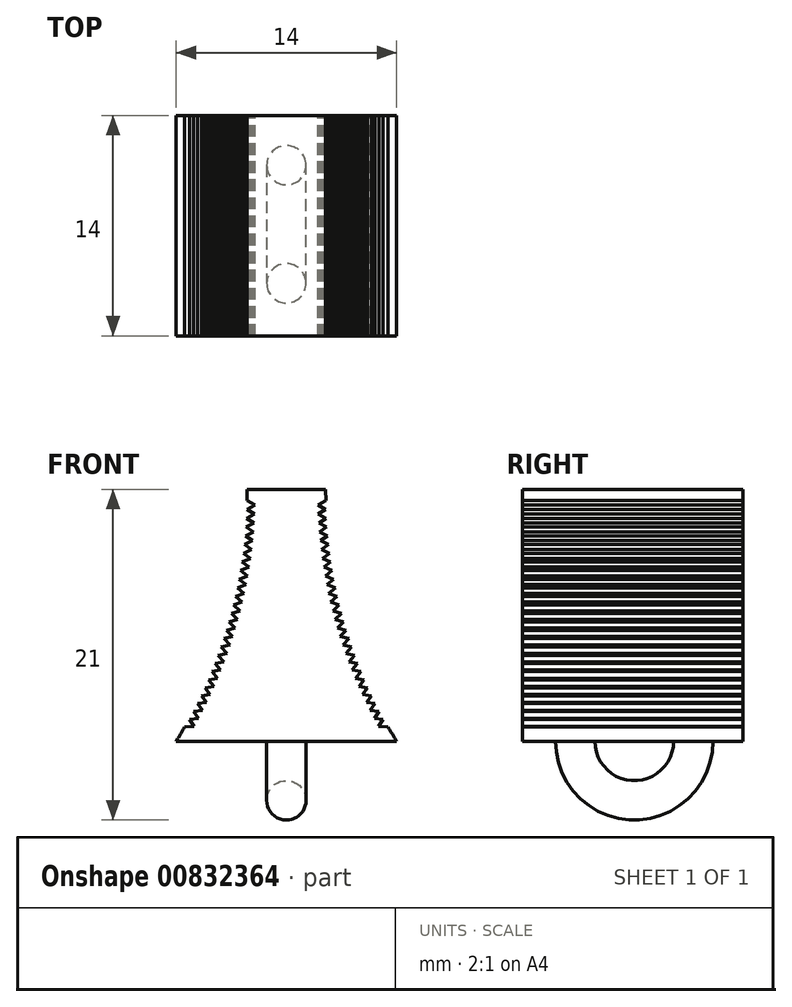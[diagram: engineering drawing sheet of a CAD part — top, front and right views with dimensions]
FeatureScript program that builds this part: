
annotation { "Feature Type Name" : "Feature", "Feature Type Description" : "" }
export const myFeature = defineFeature(function(context is Context, id is Id, definition is map)
    precondition{}
    {
        {
            var Q0;
            Q0=qCreatedBy(makeId("Front.planeOp"),FACE);
            var sketch = newSketch(context, id + "F0", { "sketchPlane" : qUnion([Q0])});
            skLineSegment(sketch, "E0.bottom", {"start": v(-7, -8) * mm, "end": v(7, -8) * mm});
            skLineSegment(sketch, "E0.top", {"start": v(-7, 8) * mm, "end": v(7, 8) * mm});
            skLineSegment(sketch, "E0.left", {"start": v(-7, -8) * mm, "end": v(-7, 8) * mm});
            skLineSegment(sketch, "E0.right", {"start": v(7, -8) * mm, "end": v(7, 8) * mm});
            skPoint(sketch, "E0.middle", {"position": v(0, 0) * mm});
            skArc(sketch, "E1", {"start": v(-7, -8) * mm, "mid": v(-3.65, -0.31) * mm, "end": v(-2.5, 8) * mm});
            skLineSegment(sketch, "E2", {"start": v(0, 8) * mm, "end": v(0, -8) * mm});
            skArc(sketch, "E3.MirrorCS", {"start": v(7, -8) * mm, "mid": v(3.65, -0.31) * mm, "end": v(2.5, 8) * mm});
            skCircle(sketch, "E4.cCircle", {"center": v(7, 7) * mm, "radius": 2.5 * mm, "construction": true});
            skLineSegment(sketch, "E4.0", {"start": v(9.5, 2.67) * mm, "end": v(2, 7) * mm});
            skLineSegment(sketch, "E4.1", {"start": v(2, 7) * mm, "end": v(9.5, 11.33) * mm});
            skLineSegment(sketch, "E4.2", {"start": v(9.5, 11.33) * mm, "end": v(9.5, 2.67) * mm});
            skPoint(sketch, "E4.0.midPoint", {"position": v(5.75, 4.83) * mm});
            skLineSegment(sketch, "E5.MirrorCS", {"start": v(-9.5, 2.67) * mm, "end": v(-2, 7) * mm});
            skLineSegment(sketch, "E6.MirrorCS", {"start": v(-2, 7) * mm, "end": v(-9.5, 11.33) * mm});
            skLineSegment(sketch, "E7.MirrorCS", {"start": v(-9.5, 11.33) * mm, "end": v(-9.5, 2.67) * mm});
            skLineSegment(sketch, "E8.1.0", {"start": v(2.02, 6.43) * mm, "end": v(9.44, 10.9) * mm});
            skLineSegment(sketch, "E8.1.1", {"start": v(9.6, 2.24) * mm, "end": v(2.02, 6.43) * mm});
            skLineSegment(sketch, "E8.1.2", {"start": v(9.44, 10.9) * mm, "end": v(9.6, 2.24) * mm});
            skLineSegment(sketch, "E8.2.0", {"start": v(2.06, 5.87) * mm, "end": v(9.4, 10.47) * mm});
            skLineSegment(sketch, "E8.2.1", {"start": v(9.7, 1.81) * mm, "end": v(2.06, 5.87) * mm});
            skLineSegment(sketch, "E8.2.2", {"start": v(9.4, 10.47) * mm, "end": v(9.7, 1.81) * mm});
            skLineSegment(sketch, "E8.3.0", {"start": v(2.1, 5.3) * mm, "end": v(9.35, 10.04) * mm});
            skLineSegment(sketch, "E8.3.1", {"start": v(9.82, 1.4) * mm, "end": v(2.1, 5.3) * mm});
            skLineSegment(sketch, "E8.3.2", {"start": v(9.35, 10.04) * mm, "end": v(9.82, 1.4) * mm});
            skLineSegment(sketch, "E8.4.0", {"start": v(2.15, 4.74) * mm, "end": v(9.32, 9.6) * mm});
            skLineSegment(sketch, "E8.4.1", {"start": v(9.95, 0.97) * mm, "end": v(2.15, 4.74) * mm});
            skLineSegment(sketch, "E8.4.2", {"start": v(9.32, 9.6) * mm, "end": v(9.95, 0.97) * mm});
            skLineSegment(sketch, "E8.5.0", {"start": v(2.22, 4.18) * mm, "end": v(9.3, 9.17) * mm});
            skLineSegment(sketch, "E8.5.1", {"start": v(10.08, 0.55) * mm, "end": v(2.22, 4.18) * mm});
            skLineSegment(sketch, "E8.5.2", {"start": v(9.3, 9.17) * mm, "end": v(10.08, 0.55) * mm});
            skLineSegment(sketch, "E8.6.0", {"start": v(2.3, 3.62) * mm, "end": v(9.28, 8.74) * mm});
            skLineSegment(sketch, "E8.6.1", {"start": v(10.22, 0.13) * mm, "end": v(2.3, 3.62) * mm});
            skLineSegment(sketch, "E8.6.2", {"start": v(9.28, 8.74) * mm, "end": v(10.22, 0.13) * mm});
            skLineSegment(sketch, "E8.7.0", {"start": v(2.38, 3.06) * mm, "end": v(9.27, 8.3) * mm});
            skLineSegment(sketch, "E8.7.1", {"start": v(10.36, -0.29) * mm, "end": v(2.38, 3.06) * mm});
            skLineSegment(sketch, "E8.7.2", {"start": v(9.27, 8.3) * mm, "end": v(10.36, -0.29) * mm});
            skLineSegment(sketch, "E8.8.0", {"start": v(2.47, 2.5) * mm, "end": v(9.27, 7.87) * mm});
            skLineSegment(sketch, "E8.8.1", {"start": v(10.52, -0.7) * mm, "end": v(2.47, 2.5) * mm});
            skLineSegment(sketch, "E8.8.2", {"start": v(9.27, 7.87) * mm, "end": v(10.52, -0.7) * mm});
            skLineSegment(sketch, "E8.9.0", {"start": v(2.58, 1.95) * mm, "end": v(9.27, 7.44) * mm});
            skLineSegment(sketch, "E8.9.1", {"start": v(10.68, -1.1) * mm, "end": v(2.58, 1.95) * mm});
            skLineSegment(sketch, "E8.9.2", {"start": v(9.27, 7.44) * mm, "end": v(10.68, -1.1) * mm});
            skLineSegment(sketch, "E8.10.0", {"start": v(2.7, 1.4) * mm, "end": v(9.29, 7) * mm});
            skLineSegment(sketch, "E8.10.1", {"start": v(10.85, -1.51) * mm, "end": v(2.7, 1.4) * mm});
            skLineSegment(sketch, "E8.10.2", {"start": v(9.29, 7) * mm, "end": v(10.85, -1.51) * mm});
            skLineSegment(sketch, "E8.11.0", {"start": v(2.82, 0.84) * mm, "end": v(9.3, 6.57) * mm});
            skLineSegment(sketch, "E8.11.1", {"start": v(11.02, -1.92) * mm, "end": v(2.82, 0.84) * mm});
            skLineSegment(sketch, "E8.11.2", {"start": v(9.3, 6.57) * mm, "end": v(11.02, -1.92) * mm});
            skLineSegment(sketch, "E8.12.0", {"start": v(2.95, 0.3) * mm, "end": v(9.34, 6.14) * mm});
            skLineSegment(sketch, "E8.12.1", {"start": v(11.2, -2.32) * mm, "end": v(2.95, 0.3) * mm});
            skLineSegment(sketch, "E8.12.2", {"start": v(9.34, 6.14) * mm, "end": v(11.2, -2.32) * mm});
            skLineSegment(sketch, "E8.13.0", {"start": v(3.1, -0.25) * mm, "end": v(9.38, 5.7) * mm});
            skLineSegment(sketch, "E8.13.1", {"start": v(11.4, -2.71) * mm, "end": v(3.1, -0.25) * mm});
            skLineSegment(sketch, "E8.13.2", {"start": v(9.38, 5.7) * mm, "end": v(11.4, -2.71) * mm});
            skLineSegment(sketch, "E8.14.0", {"start": v(3.25, -0.8) * mm, "end": v(9.42, 5.28) * mm});
            skLineSegment(sketch, "E8.14.1", {"start": v(11.6, -3.1) * mm, "end": v(3.25, -0.8) * mm});
            skLineSegment(sketch, "E8.14.2", {"start": v(9.42, 5.28) * mm, "end": v(11.6, -3.1) * mm});
            skLineSegment(sketch, "E8.15.0", {"start": v(3.41, -1.34) * mm, "end": v(9.48, 4.85) * mm});
            skLineSegment(sketch, "E8.15.1", {"start": v(11.8, -3.5) * mm, "end": v(3.41, -1.34) * mm});
            skLineSegment(sketch, "E8.15.2", {"start": v(9.48, 4.85) * mm, "end": v(11.8, -3.5) * mm});
            skLineSegment(sketch, "E8.16.0", {"start": v(3.59, -1.88) * mm, "end": v(9.54, 4.42) * mm});
            skLineSegment(sketch, "E8.16.1", {"start": v(12.01, -3.88) * mm, "end": v(3.59, -1.88) * mm});
            skLineSegment(sketch, "E8.16.2", {"start": v(9.54, 4.42) * mm, "end": v(12.01, -3.88) * mm});
            skLineSegment(sketch, "E8.17.0", {"start": v(3.77, -2.41) * mm, "end": v(9.6, 3.99) * mm});
            skLineSegment(sketch, "E8.17.1", {"start": v(12.23, -4.26) * mm, "end": v(3.77, -2.41) * mm});
            skLineSegment(sketch, "E8.17.2", {"start": v(9.6, 3.99) * mm, "end": v(12.23, -4.26) * mm});
            skLineSegment(sketch, "E8.18.0", {"start": v(3.97, -2.94) * mm, "end": v(9.68, 3.56) * mm});
            skLineSegment(sketch, "E8.18.1", {"start": v(12.46, -4.64) * mm, "end": v(3.97, -2.94) * mm});
            skLineSegment(sketch, "E8.18.2", {"start": v(9.68, 3.56) * mm, "end": v(12.46, -4.64) * mm});
            skLineSegment(sketch, "E8.19.0", {"start": v(4.17, -3.47) * mm, "end": v(9.77, 3.14) * mm});
            skLineSegment(sketch, "E8.19.1", {"start": v(12.7, -5.02) * mm, "end": v(4.17, -3.47) * mm});
            skLineSegment(sketch, "E8.19.2", {"start": v(9.77, 3.14) * mm, "end": v(12.7, -5.02) * mm});
            skLineSegment(sketch, "E8.20.0", {"start": v(4.38, -4) * mm, "end": v(9.86, 2.71) * mm});
            skLineSegment(sketch, "E8.20.1", {"start": v(12.93, -5.39) * mm, "end": v(4.38, -4) * mm});
            skLineSegment(sketch, "E8.20.2", {"start": v(9.86, 2.71) * mm, "end": v(12.93, -5.39) * mm});
            skLineSegment(sketch, "E8.21.0", {"start": v(4.6, -4.52) * mm, "end": v(9.96, 2.29) * mm});
            skLineSegment(sketch, "E8.21.1", {"start": v(13.18, -5.75) * mm, "end": v(4.6, -4.52) * mm});
            skLineSegment(sketch, "E8.21.2", {"start": v(9.96, 2.29) * mm, "end": v(13.18, -5.75) * mm});
            skLineSegment(sketch, "E8.22.0", {"start": v(4.84, -5.03) * mm, "end": v(10.07, 1.87) * mm});
            skLineSegment(sketch, "E8.22.1", {"start": v(13.43, -6.11) * mm, "end": v(4.84, -5.03) * mm});
            skLineSegment(sketch, "E8.22.2", {"start": v(10.07, 1.87) * mm, "end": v(13.43, -6.11) * mm});
            skLineSegment(sketch, "E8.23.0", {"start": v(5.08, -5.54) * mm, "end": v(10.18, 1.45) * mm});
            skLineSegment(sketch, "E8.23.1", {"start": v(13.69, -6.47) * mm, "end": v(5.08, -5.54) * mm});
            skLineSegment(sketch, "E8.23.2", {"start": v(10.18, 1.45) * mm, "end": v(13.69, -6.47) * mm});
            skLineSegment(sketch, "E8.24.0", {"start": v(5.33, -6.05) * mm, "end": v(10.3, 1.04) * mm});
            skLineSegment(sketch, "E8.24.1", {"start": v(13.95, -6.82) * mm, "end": v(5.33, -6.05) * mm});
            skLineSegment(sketch, "E8.24.2", {"start": v(10.3, 1.04) * mm, "end": v(13.95, -6.82) * mm});
            skLineSegment(sketch, "E8.25.0", {"start": v(5.59, -6.56) * mm, "end": v(10.43, 0.62) * mm});
            skLineSegment(sketch, "E8.25.1", {"start": v(14.22, -7.16) * mm, "end": v(5.59, -6.56) * mm});
            skLineSegment(sketch, "E8.25.2", {"start": v(10.43, 0.62) * mm, "end": v(14.22, -7.16) * mm});
            skLineSegment(sketch, "E8.26.0", {"start": v(5.85, -7.05) * mm, "end": v(10.57, 0.21) * mm});
            skLineSegment(sketch, "E8.26.1", {"start": v(14.5, -7.5) * mm, "end": v(5.85, -7.05) * mm});
            skLineSegment(sketch, "E8.26.2", {"start": v(10.57, 0.21) * mm, "end": v(14.5, -7.5) * mm});
            skLineSegment(sketch, "E8.anchor1", {"start": v(33.2, 8) * mm, "end": v(2, 7) * mm, "construction": true});
            skLineSegment(sketch, "E8.anchor2", {"start": v(33.2, 8) * mm, "end": v(5.85, -7.05) * mm, "construction": true});
            skLineSegment(sketch, "E9.1.0", {"start": v(-9.44, 10.9) * mm, "end": v(-9.6, 2.24) * mm});
            skLineSegment(sketch, "E9.1.1", {"start": v(-9.6, 2.24) * mm, "end": v(-2.02, 6.43) * mm});
            skLineSegment(sketch, "E9.1.2", {"start": v(-2.02, 6.43) * mm, "end": v(-9.44, 10.9) * mm});
            skLineSegment(sketch, "E9.2.0", {"start": v(-9.4, 10.47) * mm, "end": v(-9.7, 1.81) * mm});
            skLineSegment(sketch, "E9.2.1", {"start": v(-9.7, 1.81) * mm, "end": v(-2.06, 5.87) * mm});
            skLineSegment(sketch, "E9.2.2", {"start": v(-2.06, 5.87) * mm, "end": v(-9.4, 10.47) * mm});
            skLineSegment(sketch, "E9.3.0", {"start": v(-9.35, 10.04) * mm, "end": v(-9.82, 1.4) * mm});
            skLineSegment(sketch, "E9.3.1", {"start": v(-9.82, 1.4) * mm, "end": v(-2.1, 5.3) * mm});
            skLineSegment(sketch, "E9.3.2", {"start": v(-2.1, 5.3) * mm, "end": v(-9.35, 10.04) * mm});
            skLineSegment(sketch, "E9.4.0", {"start": v(-9.32, 9.6) * mm, "end": v(-9.95, 0.97) * mm});
            skLineSegment(sketch, "E9.4.1", {"start": v(-9.95, 0.97) * mm, "end": v(-2.15, 4.74) * mm});
            skLineSegment(sketch, "E9.4.2", {"start": v(-2.15, 4.74) * mm, "end": v(-9.32, 9.6) * mm});
            skLineSegment(sketch, "E9.5.0", {"start": v(-9.3, 9.17) * mm, "end": v(-10.08, 0.55) * mm});
            skLineSegment(sketch, "E9.5.1", {"start": v(-10.08, 0.55) * mm, "end": v(-2.22, 4.18) * mm});
            skLineSegment(sketch, "E9.5.2", {"start": v(-2.22, 4.18) * mm, "end": v(-9.3, 9.17) * mm});
            skLineSegment(sketch, "E9.6.0", {"start": v(-9.28, 8.74) * mm, "end": v(-10.22, 0.13) * mm});
            skLineSegment(sketch, "E9.6.1", {"start": v(-10.22, 0.13) * mm, "end": v(-2.3, 3.62) * mm});
            skLineSegment(sketch, "E9.6.2", {"start": v(-2.3, 3.62) * mm, "end": v(-9.28, 8.74) * mm});
            skLineSegment(sketch, "E9.7.0", {"start": v(-9.27, 8.3) * mm, "end": v(-10.36, -0.29) * mm});
            skLineSegment(sketch, "E9.7.1", {"start": v(-10.36, -0.29) * mm, "end": v(-2.38, 3.06) * mm});
            skLineSegment(sketch, "E9.7.2", {"start": v(-2.38, 3.06) * mm, "end": v(-9.27, 8.3) * mm});
            skLineSegment(sketch, "E9.8.0", {"start": v(-9.27, 7.87) * mm, "end": v(-10.52, -0.7) * mm});
            skLineSegment(sketch, "E9.8.1", {"start": v(-10.52, -0.7) * mm, "end": v(-2.47, 2.5) * mm});
            skLineSegment(sketch, "E9.8.2", {"start": v(-2.47, 2.5) * mm, "end": v(-9.27, 7.87) * mm});
            skLineSegment(sketch, "E9.9.0", {"start": v(-9.27, 7.44) * mm, "end": v(-10.68, -1.1) * mm});
            skLineSegment(sketch, "E9.9.1", {"start": v(-10.68, -1.1) * mm, "end": v(-2.58, 1.95) * mm});
            skLineSegment(sketch, "E9.9.2", {"start": v(-2.58, 1.95) * mm, "end": v(-9.27, 7.44) * mm});
            skLineSegment(sketch, "E9.10.0", {"start": v(-9.29, 7) * mm, "end": v(-10.85, -1.51) * mm});
            skLineSegment(sketch, "E9.10.1", {"start": v(-10.85, -1.51) * mm, "end": v(-2.7, 1.4) * mm});
            skLineSegment(sketch, "E9.10.2", {"start": v(-2.7, 1.4) * mm, "end": v(-9.29, 7) * mm});
            skLineSegment(sketch, "E9.11.0", {"start": v(-9.3, 6.57) * mm, "end": v(-11.02, -1.92) * mm});
            skLineSegment(sketch, "E9.11.1", {"start": v(-11.02, -1.92) * mm, "end": v(-2.82, 0.84) * mm});
            skLineSegment(sketch, "E9.11.2", {"start": v(-2.82, 0.84) * mm, "end": v(-9.3, 6.57) * mm});
            skLineSegment(sketch, "E9.12.0", {"start": v(-9.34, 6.14) * mm, "end": v(-11.2, -2.32) * mm});
            skLineSegment(sketch, "E9.12.1", {"start": v(-11.2, -2.32) * mm, "end": v(-2.95, 0.3) * mm});
            skLineSegment(sketch, "E9.12.2", {"start": v(-2.95, 0.3) * mm, "end": v(-9.34, 6.14) * mm});
            skLineSegment(sketch, "E9.13.0", {"start": v(-9.38, 5.7) * mm, "end": v(-11.4, -2.71) * mm});
            skLineSegment(sketch, "E9.13.1", {"start": v(-11.4, -2.71) * mm, "end": v(-3.1, -0.25) * mm});
            skLineSegment(sketch, "E9.13.2", {"start": v(-3.1, -0.25) * mm, "end": v(-9.38, 5.7) * mm});
            skLineSegment(sketch, "E9.14.0", {"start": v(-9.42, 5.28) * mm, "end": v(-11.6, -3.1) * mm});
            skLineSegment(sketch, "E9.14.1", {"start": v(-11.6, -3.1) * mm, "end": v(-3.25, -0.8) * mm});
            skLineSegment(sketch, "E9.14.2", {"start": v(-3.25, -0.8) * mm, "end": v(-9.42, 5.28) * mm});
            skLineSegment(sketch, "E9.15.0", {"start": v(-9.48, 4.85) * mm, "end": v(-11.8, -3.5) * mm});
            skLineSegment(sketch, "E9.15.1", {"start": v(-11.8, -3.5) * mm, "end": v(-3.41, -1.34) * mm});
            skLineSegment(sketch, "E9.15.2", {"start": v(-3.41, -1.34) * mm, "end": v(-9.48, 4.85) * mm});
            skLineSegment(sketch, "E9.16.0", {"start": v(-9.54, 4.42) * mm, "end": v(-12.01, -3.88) * mm});
            skLineSegment(sketch, "E9.16.1", {"start": v(-12.01, -3.88) * mm, "end": v(-3.59, -1.88) * mm});
            skLineSegment(sketch, "E9.16.2", {"start": v(-3.59, -1.88) * mm, "end": v(-9.54, 4.42) * mm});
            skLineSegment(sketch, "E9.17.0", {"start": v(-9.6, 3.99) * mm, "end": v(-12.23, -4.26) * mm});
            skLineSegment(sketch, "E9.17.1", {"start": v(-12.23, -4.26) * mm, "end": v(-3.77, -2.41) * mm});
            skLineSegment(sketch, "E9.17.2", {"start": v(-3.77, -2.41) * mm, "end": v(-9.6, 3.99) * mm});
            skLineSegment(sketch, "E9.18.0", {"start": v(-9.68, 3.56) * mm, "end": v(-12.46, -4.64) * mm});
            skLineSegment(sketch, "E9.18.1", {"start": v(-12.46, -4.64) * mm, "end": v(-3.97, -2.94) * mm});
            skLineSegment(sketch, "E9.18.2", {"start": v(-3.97, -2.94) * mm, "end": v(-9.68, 3.56) * mm});
            skLineSegment(sketch, "E9.19.0", {"start": v(-9.77, 3.14) * mm, "end": v(-12.7, -5.02) * mm});
            skLineSegment(sketch, "E9.19.1", {"start": v(-12.7, -5.02) * mm, "end": v(-4.17, -3.47) * mm});
            skLineSegment(sketch, "E9.19.2", {"start": v(-4.17, -3.47) * mm, "end": v(-9.77, 3.14) * mm});
            skLineSegment(sketch, "E9.20.0", {"start": v(-9.86, 2.71) * mm, "end": v(-12.93, -5.39) * mm});
            skLineSegment(sketch, "E9.20.1", {"start": v(-12.93, -5.39) * mm, "end": v(-4.38, -4) * mm});
            skLineSegment(sketch, "E9.20.2", {"start": v(-4.38, -4) * mm, "end": v(-9.86, 2.71) * mm});
            skLineSegment(sketch, "E9.21.0", {"start": v(-9.96, 2.29) * mm, "end": v(-13.18, -5.75) * mm});
            skLineSegment(sketch, "E9.21.1", {"start": v(-13.18, -5.75) * mm, "end": v(-4.6, -4.52) * mm});
            skLineSegment(sketch, "E9.21.2", {"start": v(-4.6, -4.52) * mm, "end": v(-9.96, 2.29) * mm});
            skLineSegment(sketch, "E9.22.0", {"start": v(-10.07, 1.87) * mm, "end": v(-13.43, -6.11) * mm});
            skLineSegment(sketch, "E9.22.1", {"start": v(-13.43, -6.11) * mm, "end": v(-4.84, -5.03) * mm});
            skLineSegment(sketch, "E9.22.2", {"start": v(-4.84, -5.03) * mm, "end": v(-10.07, 1.87) * mm});
            skLineSegment(sketch, "E9.23.0", {"start": v(-10.18, 1.45) * mm, "end": v(-13.69, -6.47) * mm});
            skLineSegment(sketch, "E9.23.1", {"start": v(-13.69, -6.47) * mm, "end": v(-5.08, -5.54) * mm});
            skLineSegment(sketch, "E9.23.2", {"start": v(-5.08, -5.54) * mm, "end": v(-10.18, 1.45) * mm});
            skLineSegment(sketch, "E9.24.0", {"start": v(-10.3, 1.04) * mm, "end": v(-13.95, -6.82) * mm});
            skLineSegment(sketch, "E9.24.1", {"start": v(-13.95, -6.82) * mm, "end": v(-5.33, -6.05) * mm});
            skLineSegment(sketch, "E9.24.2", {"start": v(-5.33, -6.05) * mm, "end": v(-10.3, 1.04) * mm});
            skLineSegment(sketch, "E9.25.0", {"start": v(-10.43, 0.62) * mm, "end": v(-14.22, -7.16) * mm});
            skLineSegment(sketch, "E9.25.1", {"start": v(-14.22, -7.16) * mm, "end": v(-5.59, -6.56) * mm});
            skLineSegment(sketch, "E9.25.2", {"start": v(-5.59, -6.56) * mm, "end": v(-10.43, 0.62) * mm});
            skLineSegment(sketch, "E9.26.0", {"start": v(-10.57, 0.21) * mm, "end": v(-14.5, -7.5) * mm});
            skLineSegment(sketch, "E9.26.1", {"start": v(-14.5, -7.5) * mm, "end": v(-5.85, -7.05) * mm});
            skLineSegment(sketch, "E9.26.2", {"start": v(-5.85, -7.05) * mm, "end": v(-10.57, 0.21) * mm});
            skLineSegment(sketch, "E9.anchor1", {"start": v(-33.2, 8) * mm, "end": v(-9.5, 2.67) * mm, "construction": true});
            skLineSegment(sketch, "E9.anchor2", {"start": v(-33.2, 8) * mm, "end": v(-14.5, -7.5) * mm, "construction": true});
            skSolve(sketch);
        }
        {
            var Q0;
            {var subQ80=sQuery(id+"F0.wireOp",EDGE,"E2");Q0=makeQuery(id+"F0.imprint","IMPRINT",FACE,{"disambiguationData":[TD([[makeQuery(id+"F0.imprint","IMPRINT",EDGE,{"derivedFrom":subQ80}),1.0]])]});}
            var Q1;
            {var subQ76=sQuery(id+"F0.wireOp",EDGE,"E2");Q1=makeQuery(id+"F0.imprint","IMPRINT",FACE,{"disambiguationData":[TD([[makeQuery(id+"F0.imprint","IMPRINT",EDGE,{"derivedFrom":subQ76}),-1.0]])]});}
            extrude(context, id + "F1", {"entities" : qUnion([Q0, Q1]), "depth" : 14 * mm, "offsetDistance" : 25 * mm});
        }
        {
            var Q0;
            Q0=qCreatedBy(makeId("Right.planeOp"),FACE);
            var sketch = newSketch(context, id + "F2", { "sketchPlane" : qUnion([Q0])});
            skArc(sketch, "E10", {"start": v(-11.9, -8) * mm, "mid": v(-6.9, -13) * mm, "end": v(-1.9, -8) * mm});
            skArc(sketch, "E11", {"start": v(-9.4, -8) * mm, "mid": v(-6.9, -10.5) * mm, "end": v(-4.4, -8) * mm});
            skLineSegment(sketch, "E12", {"start": v(-11.9, -8) * mm, "end": v(-1.9, -8) * mm});
            skSolve(sketch);
        }
        {
            var Q0;
            {var subQ0=sQuery(id+"F2.wireOp",EDGE,"E10");Q0=makeQuery(id+"F2.imprint","IMPRINT",FACE,{"disambiguationData":[TD([[makeQuery(id+"F2.imprint","IMPRINT",EDGE,{"derivedFrom":subQ0}),1.0]])]});}
            extrude(context, id + "F3", {"entities" : qUnion([Q0]), "operationType" : NewBodyOperationType.ADD, "endBound" : BoundingType.SYMMETRIC, "depth" : 2.5 * mm, "offsetDistance" : 25 * mm});
        }
        {
            var Q0;
            Q0=makeQuery(id+"F3.opExtrude","CAP_EDGE",EDGE,{"disambiguationData":[OSD([sQuery(id+"F2.wireOp",EDGE,"E10")])],"isStart":false});
            var Q1;
            Q1=makeQuery(id+"F3.opExtrude","CAP_EDGE",EDGE,{"disambiguationData":[OSD([sQuery(id+"F2.wireOp",EDGE,"E10")])],"isStart":true});
            var Q2;
            Q2=makeQuery(id+"F3.opExtrude","CAP_EDGE",EDGE,{"disambiguationData":[OSD([sQuery(id+"F2.wireOp",EDGE,"E11")])],"isStart":false});
            var Q3;
            Q3=makeQuery(id+"F3.opExtrude","CAP_EDGE",EDGE,{"disambiguationData":[OSD([sQuery(id+"F2.wireOp",EDGE,"E11")])],"isStart":true});
            fillet(context, id + "F4", {"entities" : qUnion([Q0, Q1, Q2, Q3]), "radius" : 1.25 * mm, "tangentPropagation" : true, "allowEdgeOverflow" : false});
        }
    });
